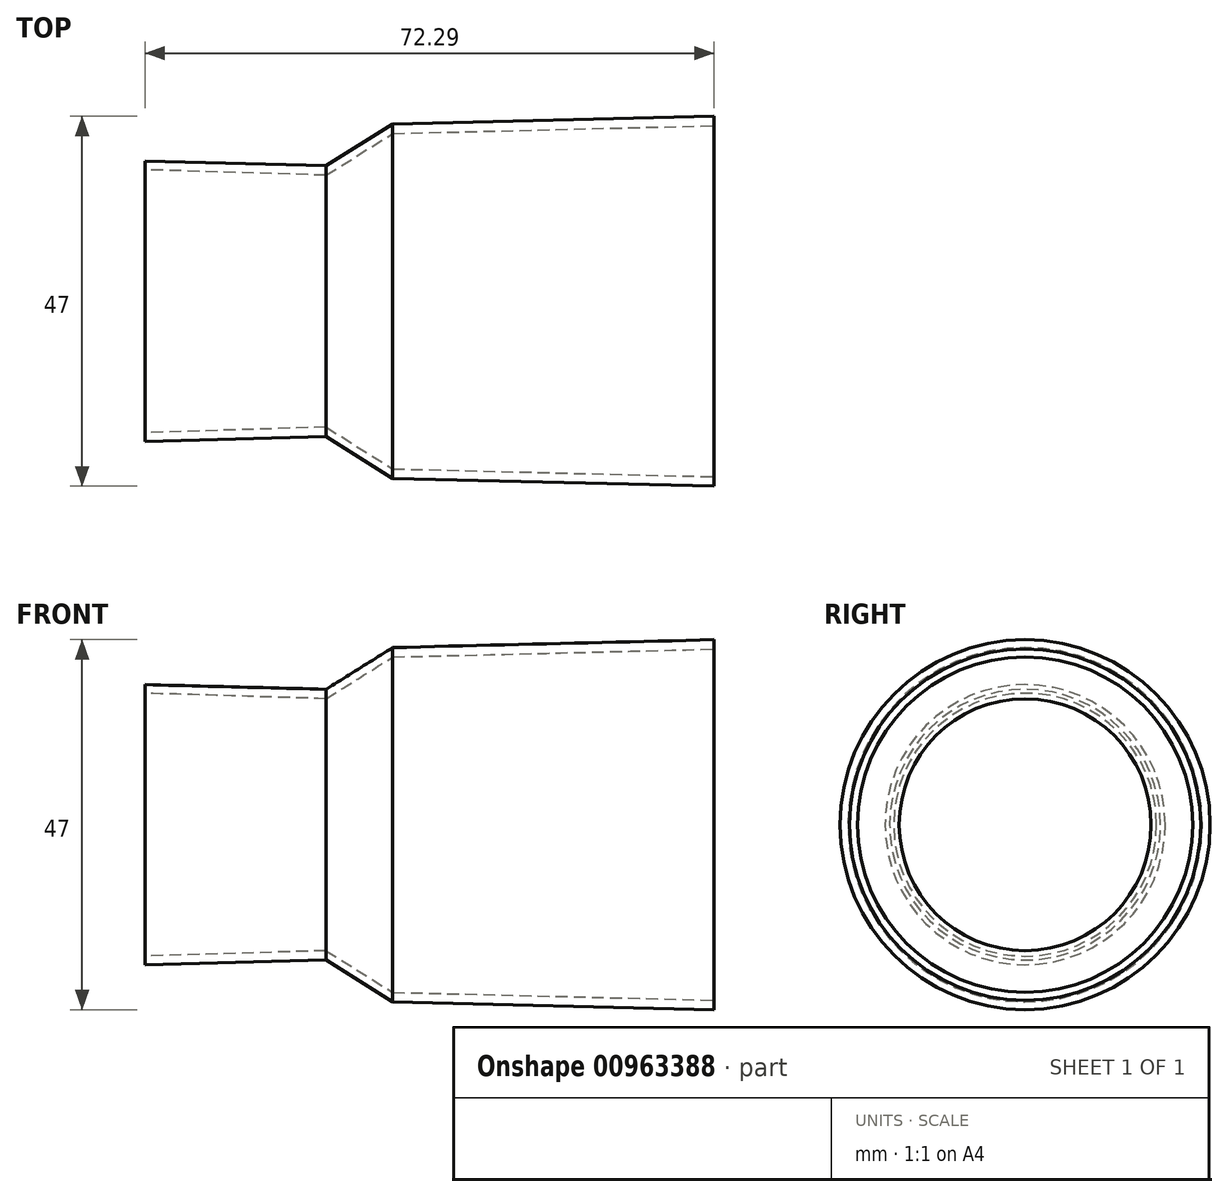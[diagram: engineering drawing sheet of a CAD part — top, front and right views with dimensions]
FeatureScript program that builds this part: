
annotation { "Feature Type Name" : "Feature", "Feature Type Description" : "" }
export const myFeature = defineFeature(function(context is Context, id is Id, definition is map)
    precondition{}
    {
        {
            var Q0;
            Q0=qCreatedBy(makeId("Top.planeOp"),FACE);
            var sketch = newSketch(context, id + "F0", { "sketchPlane" : qUnion([Q0])});
            skLineSegment(sketch, "E0", {"start": v(2.23, 21.3) * mm, "end": v(-6.25, 16) * mm});
            skLineSegment(sketch, "E1", {"start": v(-29.24, 16.14) * mm, "end": v(-29.24, 16.7) * mm});
            skLineSegment(sketch, "E2", {"start": v(-6.25, 17.2) * mm, "end": v(2.23, 22.5) * mm});
            skLineSegment(sketch, "E3", {"start": v(-43.34, 0) * mm, "end": v(39.1, 0) * mm, "construction": true});
            skLineSegment(sketch, "E4", {"start": v(2.23, 22.5) * mm, "end": v(43.02, 23.5) * mm});
            skLineSegment(sketch, "E5", {"start": v(43.02, 23.5) * mm, "end": v(43.05, 22.3) * mm});
            skLineSegment(sketch, "E6", {"start": v(43.05, 22.3) * mm, "end": v(2.23, 21.3) * mm});
            skPoint(sketch, "E7", {"position": v(43.05, 22.3) * mm});
            skPoint(sketch, "E8", {"position": v(22.64, 21.8) * mm});
            skPoint(sketch, "E9", {"position": v(2.23, 21.3) * mm});
            skLineSegment(sketch, "E10", {"start": v(43.05, 22.3) * mm, "end": v(43.05, 0) * mm, "construction": true});
            skLineSegment(sketch, "E11", {"start": v(2.23, 21.3) * mm, "end": v(2.23, 0) * mm, "construction": true});
            skLineSegment(sketch, "E12", {"start": v(-6.25, 16) * mm, "end": v(-6.25, 0) * mm, "construction": true});
            skLineSegment(sketch, "E13", {"start": v(-29.24, 16.7) * mm, "end": v(-29.24, 0) * mm, "construction": true});
            skLineSegment(sketch, "E14", {"start": v(-29.24, 16.7) * mm, "end": v(-6.25, 16) * mm});
            skLineSegment(sketch, "E15", {"start": v(-6.25, 17.2) * mm, "end": v(-6.25, 16) * mm, "construction": true});
            skLineSegment(sketch, "E16", {"start": v(-29.24, 16.7) * mm, "end": v(-29.24, 17.8) * mm});
            skLineSegment(sketch, "E17", {"start": v(-29.24, 17.8) * mm, "end": v(-6.25, 17.2) * mm});
            skLineSegment(sketch, "E18", {"start": v(2.23, 22.5) * mm, "end": v(2.23, 21.3) * mm, "construction": true});
            skSolve(sketch);
        }
        {
            var Q0;
            Q0=makeQuery(id+"F0.imprint","IMPRINT",FACE,{"disambiguationData":[TD([[makeQuery(id+"F0.imprint","IMPRINT",EDGE,{"derivedFrom":sQuery(id+"F0.wireOp",EDGE,"E0")}),-1.0]])]});
            var Q1;
            Q1=sQuery(id+"F0.wireOp",EDGE,"E3");
            revolve(context, id + "F1", {"surfaceOperationType" : NewSurfaceOperationType.NEW, "entities" : qUnion([Q0]), "axis" : qUnion([Q1]), "revolveType" : RevolveType.FULL});
        }
    });
